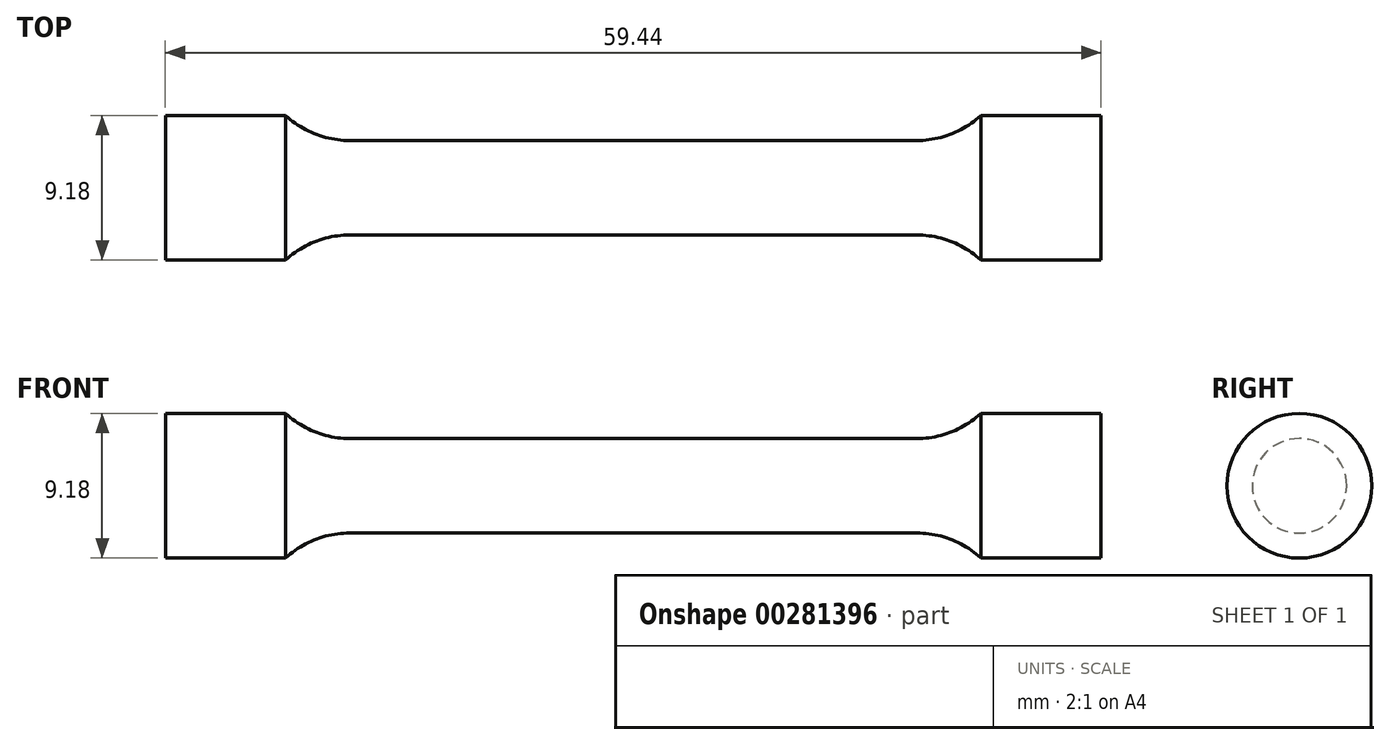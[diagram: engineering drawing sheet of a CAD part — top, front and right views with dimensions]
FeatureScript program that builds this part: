
annotation { "Feature Type Name" : "Feature", "Feature Type Description" : "" }
export const myFeature = defineFeature(function(context is Context, id is Id, definition is map)
    precondition{}
    {
        {
            var Q0;
            Q0=qCreatedBy(makeId("Front.planeOp"),FACE);
            var sketch = newSketch(context, id + "F0", { "sketchPlane" : qUnion([Q0])});
            skLineSegment(sketch, "E0", {"start": v(0, 3) * mm, "end": v(18, 3) * mm});
            skArc(sketch, "E1", {"start": v(18, 3) * mm, "mid": v(20.19, 3.41) * mm, "end": v(22.07, 4.6) * mm});
            skLineSegment(sketch, "E2", {"start": v(22.07, 4.6) * mm, "end": v(29.72, 4.6) * mm});
            skLineSegment(sketch, "E3", {"start": v(29.72, 4.6) * mm, "end": v(29.72, 0) * mm});
            skLineSegment(sketch, "E4", {"start": v(0, 0) * mm, "end": v(29.72, 0) * mm});
            skLineSegment(sketch, "E5.MirrorCS", {"start": v(0, 3) * mm, "end": v(-18, 3) * mm});
            skLineSegment(sketch, "E6.MirrorCS", {"start": v(0, 0) * mm, "end": v(-29.72, 0) * mm});
            skLineSegment(sketch, "E7.MirrorCS", {"start": v(-22.07, 4.6) * mm, "end": v(-29.72, 4.6) * mm});
            skLineSegment(sketch, "E8.MirrorCS", {"start": v(-29.72, 4.6) * mm, "end": v(-29.72, 0) * mm});
            skArc(sketch, "E9.MirrorCS", {"start": v(-18, 3) * mm, "mid": v(-20.19, 3.41) * mm, "end": v(-22.07, 4.6) * mm});
            skSolve(sketch);
        }
        {
            var Q0;
            Q0 = qSketchRegion(id + "F0", true);
            var Q1;
            Q1=sQuery(id+"F0.wireOp",EDGE,"E4");
            revolve(context, id + "F1", {"entities" : qUnion([Q0]), "axis" : qUnion([Q1]), "revolveType" : RevolveType.FULL});
        }
    });
